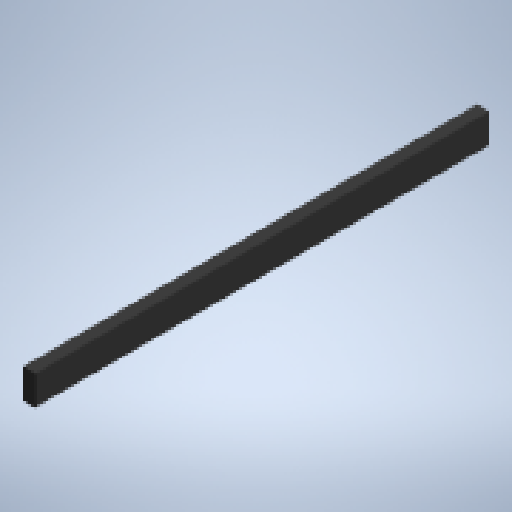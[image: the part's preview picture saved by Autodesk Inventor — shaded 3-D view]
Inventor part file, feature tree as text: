
AUTODESK INVENTOR PART (.ipt)
format: ipt  version: 2023 (Build 270158000, 158)  size: 154,624 bytes
history: native  units: in
note: dims shown in document units (in); Inventor stores cm internally (conversion verified against a paired STEP export)
features: extrude x1, sketch x1
ambient origin geometry x8: Origin, YZ Plane, XZ Plane, XY Plane, X Axis, Y Axis, Z Axis, Center Point
bodies: Solid1 (feature_tree)
feature tree (2):
  extrude  "Extrusion1"  Depth=3.5in
  sketch  "Sketch1"  dims[d0=1.5in d1=3.5in d2=0.125in d3=53.0in d4=0.0in]
